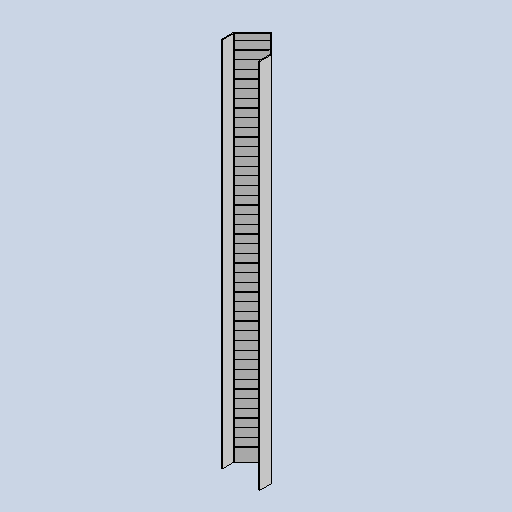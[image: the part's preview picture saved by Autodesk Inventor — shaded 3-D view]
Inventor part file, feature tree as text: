
AUTODESK INVENTOR PART (.ipt)
format: ipt  version: 2025.3 (Build 293356030, 356C)  size: 912,896 bytes
history: native  units: mm
features: sheet_metal_op x3, sketch x3, other x3, mirror x1
ambient origin geometry x8: Origin, YZ Plane, XZ Plane, XY Plane, X Axis, Y Axis, Z Axis, Center Point
bodies: Body1 (feature_tree)
feature tree (10):
  sheet_metal_op  "Contour Flange1"
  mirror  "Mirror2"
  sketch  "Sketch3"  dims[d15=10.0mm]
  other  "Plate1"
  sheet_metal_op  "Bend1"
  sheet_metal_op  "Corner1"
  sketch  "Sketch5"  dims[d19=1.0mm d20=1.0mm d21=0.8mm d22=0.8mm d23=0.4mm d24=1.6mm d25=0.8mm d26=310.0mm d27=0.8mm d28=0.8mm d29=3.2mm d30=0.8mm d31=0.8mm d32=32.0mm d33=90.0deg d111=0.2mm d112=20.0mm d113=5.0mm d114=0.5mm d115=435.714286mm d116=7.0mm d73=10.0mm d75=10.0mm d97=5.0mm d98=0.8mm d99=0.0mm d101=0.5mm d102=0.872665mm d103=0.5mm d104=0.872665mm]
  sketch  "Sketch Rectangular Pattern3"  dims[d18=1.0mm]
  other  "Cut3"
  other  "Definition1"
